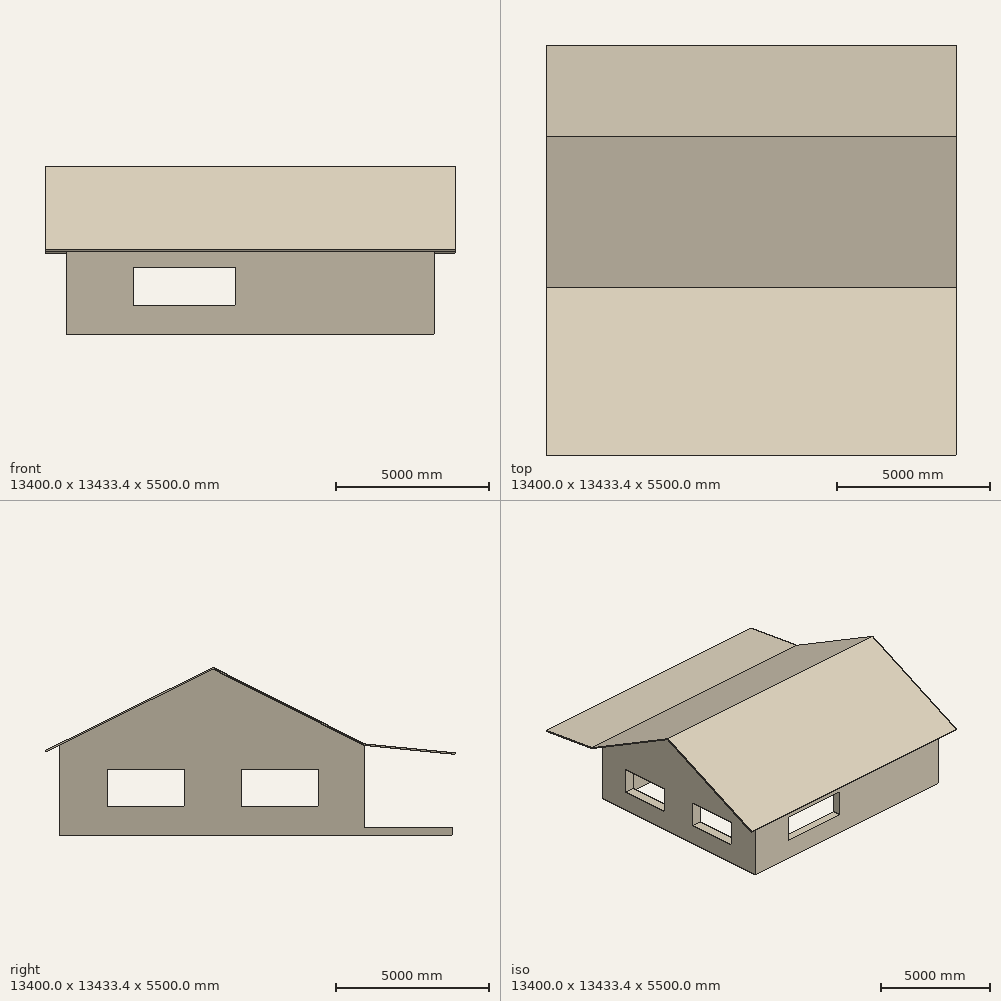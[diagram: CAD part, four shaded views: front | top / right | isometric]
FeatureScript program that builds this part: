
annotation { "Feature Type Name" : "Feature", "Feature Type Description" : "" }
export const myFeature = defineFeature(function(context is Context, id is Id, definition is map)
    precondition{}
    {
        {
            var Q0;
            Q0=qCreatedBy(makeId("Right.planeOp"),FACE);
            var sketch = newSketch(context, id + "F0", { "sketchPlane" : qUnion([Q0])});
            skLineSegment(sketch, "E0.bottom", {"start": v(-5048.67, 0) * mm, "end": v(4951.33, 0) * mm});
            skLineSegment(sketch, "E0.top", {"start": v(-5048.67, 0) * mm, "end": v(4951.33, 0) * mm});
            skLineSegment(sketch, "E0.left", {"start": v(-5048.67, 0) * mm, "end": v(-5048.67, 0) * mm});
            skLineSegment(sketch, "E0.right", {"start": v(4951.33, 0) * mm, "end": v(4951.33, 0) * mm});
            skLineSegment(sketch, "E1", {"start": v(4951.33, 250) * mm, "end": v(4951.33, 2949.75) * mm});
            skLineSegment(sketch, "E2", {"start": v(4951.33, 3000) * mm, "end": v(0, 5500) * mm});
            skLineSegment(sketch, "E3", {"start": v(0, 5500) * mm, "end": v(-5048.67, 3000) * mm});
            skLineSegment(sketch, "E4", {"start": v(-5048.67, 2944.2) * mm, "end": v(-5048.67, 0) * mm});
            skLineSegment(sketch, "E5", {"start": v(-5048.67, 3000) * mm, "end": v(-5496.74, 2778.12) * mm});
            skLineSegment(sketch, "E6", {"start": v(-5496.74, 2778.12) * mm, "end": v(-5474.56, 2733.32) * mm});
            skLineSegment(sketch, "E7", {"start": v(-5474.56, 2733.32) * mm, "end": v(-5048.67, 2944.2) * mm});
            skLineSegment(sketch, "E8", {"start": v(4951.33, 3000) * mm, "end": v(7936.67, 2703.75) * mm});
            skLineSegment(sketch, "E9", {"start": v(7936.67, 2703.75) * mm, "end": v(7931.73, 2654) * mm});
            skLineSegment(sketch, "E10", {"start": v(7931.73, 2654) * mm, "end": v(4951.33, 2949.75) * mm});
            skLineSegment(sketch, "E11", {"start": v(4951.33, 0) * mm, "end": v(7851.33, 0) * mm});
            skLineSegment(sketch, "E12", {"start": v(7851.33, 0) * mm, "end": v(7851.33, 250) * mm});
            skLineSegment(sketch, "E13", {"start": v(7851.33, 250) * mm, "end": v(4951.33, 250) * mm});
            skSolve(sketch);
        }
        {
            var Q0;
            Q0 = qSketchRegion(id + "F0", true);
            extrude(context, id + "F1", {"entities" : qUnion([Q0]), "depth" : 12000 * mm, "offsetDistance" : 25 * mm});
        }
        {
            var Q0;
            Q0=makeQuery(id+"F1.opExtrude","SWEPT_FACE",FACE,{"disambiguationData":[OSD([sQuery(id+"F0.wireOp",EDGE,"E0.top"),sQuery(id+"F0.wireOp",EDGE,"E11")])]});
            var sketch = newSketch(context, id + "F2", { "sketchPlane" : qUnion([Q0])});
            skLineSegment(sketch, "E14", {"start": v(0, -7851.33) * mm, "end": v(0, -4951.33) * mm});
            skLineSegment(sketch, "E15", {"start": v(0, -4951.33) * mm, "end": v(5000, -4951.33) * mm});
            skLineSegment(sketch, "E16", {"start": v(5000, -4951.33) * mm, "end": v(5000, -7851.33) * mm});
            skLineSegment(sketch, "E17", {"start": v(5000, -7851.33) * mm, "end": v(0, -7851.33) * mm});
            skSolve(sketch);
        }
        {
            var Q0;
            Q0 = qSketchRegion(id + "F2", true);
            extrude(context, id + "F3", {"entities" : qUnion([Q0]), "operationType" : NewBodyOperationType.REMOVE, "oppositeDirection" : true, "depth" : 250 * mm, "offsetDistance" : 25 * mm});
        }
        {
            var Q0;
            Q0=makeQuery(id+"F1.opExtrude","CAP_FACE",FACE,{"disambiguationData":[OSD([sQuery(id+"F0.wireOp",EDGE,"E0.top"),sQuery(id+"F0.wireOp",EDGE,"E1"),sQuery(id+"F0.wireOp",EDGE,"E2"),sQuery(id+"F0.wireOp",EDGE,"E3"),sQuery(id+"F0.wireOp",EDGE,"E4"),sQuery(id+"F0.wireOp",EDGE,"E5"),sQuery(id+"F0.wireOp",EDGE,"E6"),sQuery(id+"F0.wireOp",EDGE,"E7"),sQuery(id+"F0.wireOp",EDGE,"E8"),sQuery(id+"F0.wireOp",EDGE,"E9"),sQuery(id+"F0.wireOp",EDGE,"E10"),sQuery(id+"F0.wireOp",EDGE,"E11"),sQuery(id+"F0.wireOp",EDGE,"E12"),sQuery(id+"F0.wireOp",EDGE,"E13")])],"isStart":true});
            var sketch = newSketch(context, id + "F4", { "sketchPlane" : qUnion([Q0])});
            skLineSegment(sketch, "E18", {"start": v(5496.74, 2778.12) * mm, "end": v(0, 5500) * mm});
            skLineSegment(sketch, "E19", {"start": v(0, 5500) * mm, "end": v(-4951.33, 3000) * mm});
            skLineSegment(sketch, "E20", {"start": v(-4951.33, 3000) * mm, "end": v(-7936.67, 2703.75) * mm});
            skLineSegment(sketch, "E21", {"start": v(-7936.67, 2703.75) * mm, "end": v(-7931.73, 2654) * mm});
            skLineSegment(sketch, "E22", {"start": v(-7931.73, 2654) * mm, "end": v(-4951.33, 2949.75) * mm});
            skLineSegment(sketch, "E23", {"start": v(-4951.33, 2949.75) * mm, "end": v(0, 5449.75) * mm});
            skLineSegment(sketch, "E24", {"start": v(0, 5449.75) * mm, "end": v(5474.56, 2733.32) * mm});
            skLineSegment(sketch, "E25", {"start": v(5474.56, 2733.32) * mm, "end": v(5496.74, 2778.12) * mm});
            skSolve(sketch);
        }
        {
            var Q0;
            Q0 = qSketchRegion(id + "F4", true);
            extrude(context, id + "F5", {"entities" : qUnion([Q0]), "operationType" : NewBodyOperationType.ADD, "depth" : 700 * mm, "offsetDistance" : 25 * mm});
        }
        {
            var Q0;
            Q0=makeQuery(id+"F1.opExtrude","CAP_FACE",FACE,{"disambiguationData":[OSD([sQuery(id+"F0.wireOp",EDGE,"E0.top"),sQuery(id+"F0.wireOp",EDGE,"E1"),sQuery(id+"F0.wireOp",EDGE,"E2"),sQuery(id+"F0.wireOp",EDGE,"E3"),sQuery(id+"F0.wireOp",EDGE,"E4"),sQuery(id+"F0.wireOp",EDGE,"E5"),sQuery(id+"F0.wireOp",EDGE,"E6"),sQuery(id+"F0.wireOp",EDGE,"E7"),sQuery(id+"F0.wireOp",EDGE,"E8"),sQuery(id+"F0.wireOp",EDGE,"E9"),sQuery(id+"F0.wireOp",EDGE,"E10"),sQuery(id+"F0.wireOp",EDGE,"E11"),sQuery(id+"F0.wireOp",EDGE,"E12"),sQuery(id+"F0.wireOp",EDGE,"E13")])],"isStart":false});
            var sketch = newSketch(context, id + "F6", { "sketchPlane" : qUnion([Q0])});
            skLineSegment(sketch, "E26", {"start": v(-5474.56, 2733.32) * mm, "end": v(-5496.74, 2778.12) * mm});
            skLineSegment(sketch, "E27", {"start": v(-5496.74, 2778.12) * mm, "end": v(0, 5500) * mm});
            skLineSegment(sketch, "E28", {"start": v(0, 5500) * mm, "end": v(4951.33, 3000) * mm});
            skLineSegment(sketch, "E29", {"start": v(4951.33, 3000) * mm, "end": v(7936.67, 2703.75) * mm});
            skLineSegment(sketch, "E30", {"start": v(7936.67, 2703.75) * mm, "end": v(7931.73, 2654) * mm});
            skLineSegment(sketch, "E31", {"start": v(7931.73, 2654) * mm, "end": v(4951.33, 2949.75) * mm});
            skLineSegment(sketch, "E32", {"start": v(4951.33, 2949.75) * mm, "end": v(0, 5449.75) * mm});
            skLineSegment(sketch, "E33", {"start": v(0, 5449.75) * mm, "end": v(-5474.56, 2733.32) * mm});
            skSolve(sketch);
        }
        {
            var Q0;
            Q0 = qSketchRegion(id + "F6", true);
            extrude(context, id + "F7", {"entities" : qUnion([Q0]), "operationType" : NewBodyOperationType.ADD, "depth" : 700 * mm, "offsetDistance" : 25 * mm});
        }
        {
            var Q0;
            Q0=makeQuery(id+"F1.opExtrude","SWEPT_FACE",FACE,{"disambiguationData":[OSD([sQuery(id+"F0.wireOp",EDGE,"E0.top"),sQuery(id+"F0.wireOp",EDGE,"E11")])]});
            var sketch = newSketch(context, id + "F8", { "sketchPlane" : qUnion([Q0])});
            skLineSegment(sketch, "E34.bottom", {"start": v(500, 4648.67) * mm, "end": v(11500, 4648.67) * mm});
            skLineSegment(sketch, "E34.top", {"start": v(500, -4451.33) * mm, "end": v(11500, -4451.33) * mm});
            skLineSegment(sketch, "E34.left", {"start": v(500, 4648.67) * mm, "end": v(500, -4451.33) * mm});
            skLineSegment(sketch, "E34.right", {"start": v(11500, 4648.67) * mm, "end": v(11500, -4451.33) * mm});
            skSolve(sketch);
        }
        {
            var Q0;
            Q0 = qSketchRegion(id + "F8", true);
            extrude(context, id + "F9", {"entities" : qUnion([Q0]), "operationType" : NewBodyOperationType.REMOVE, "oppositeDirection" : true, "depth" : 2950 * mm, "offsetDistance" : 25 * mm});
        }
        {
            var Q0;
            Q0=makeQuery(id+"F1.opExtrude","CAP_FACE",FACE,{"disambiguationData":[OSD([sQuery(id+"F0.wireOp",EDGE,"E0.top"),sQuery(id+"F0.wireOp",EDGE,"E1"),sQuery(id+"F0.wireOp",EDGE,"E2"),sQuery(id+"F0.wireOp",EDGE,"E3"),sQuery(id+"F0.wireOp",EDGE,"E4"),sQuery(id+"F0.wireOp",EDGE,"E5"),sQuery(id+"F0.wireOp",EDGE,"E6"),sQuery(id+"F0.wireOp",EDGE,"E7"),sQuery(id+"F0.wireOp",EDGE,"E8"),sQuery(id+"F0.wireOp",EDGE,"E9"),sQuery(id+"F0.wireOp",EDGE,"E10"),sQuery(id+"F0.wireOp",EDGE,"E11"),sQuery(id+"F0.wireOp",EDGE,"E12"),sQuery(id+"F0.wireOp",EDGE,"E13")])],"isStart":true});
            var sketch = newSketch(context, id + "F10", { "sketchPlane" : qUnion([Q0])});
            skLineSegment(sketch, "E35.bottom", {"start": v(-3453.27, 949.36) * mm, "end": v(-933.16, 949.36) * mm});
            skLineSegment(sketch, "E35.top", {"start": v(-3453.27, 2162.4) * mm, "end": v(-933.16, 2162.4) * mm});
            skLineSegment(sketch, "E35.left", {"start": v(-3453.27, 949.36) * mm, "end": v(-3453.27, 2162.4) * mm});
            skLineSegment(sketch, "E35.right", {"start": v(-933.16, 949.36) * mm, "end": v(-933.16, 2162.4) * mm});
            skLineSegment(sketch, "E36.MirrorCS", {"start": v(3453.27, 949.36) * mm, "end": v(3453.27, 2162.4) * mm});
            skLineSegment(sketch, "E37.MirrorCS", {"start": v(933.16, 949.36) * mm, "end": v(933.16, 2162.4) * mm});
            skLineSegment(sketch, "E38.MirrorCS", {"start": v(3453.27, 949.36) * mm, "end": v(933.16, 949.36) * mm});
            skLineSegment(sketch, "E39.MirrorCS", {"start": v(3453.27, 2162.4) * mm, "end": v(933.16, 2162.4) * mm});
            skSolve(sketch);
        }
        {
            var Q0;
            Q0 = qSketchRegion(id + "F10", true);
            extrude(context, id + "F11", {"entities" : qUnion([Q0]), "operationType" : NewBodyOperationType.REMOVE, "oppositeDirection" : true, "depth" : 12000 * mm, "offsetDistance" : 25 * mm});
        }
        {
            var Q0;
            Q0=makeQuery(id+"F1.opExtrude","SWEPT_FACE",FACE,{"disambiguationData":[OSD([sQuery(id+"F0.wireOp",EDGE,"E4")])]});
            var sketch = newSketch(context, id + "F12", { "sketchPlane" : qUnion([Q0])});
            skLineSegment(sketch, "E40.bottom", {"start": v(2167.56, 2201.24) * mm, "end": v(5521.46, 2201.24) * mm});
            skLineSegment(sketch, "E40.top", {"start": v(2167.56, 966.02) * mm, "end": v(5521.46, 966.02) * mm});
            skLineSegment(sketch, "E40.left", {"start": v(2167.56, 2201.24) * mm, "end": v(2167.56, 966.02) * mm});
            skLineSegment(sketch, "E40.right", {"start": v(5521.46, 2201.24) * mm, "end": v(5521.46, 966.02) * mm});
            skSolve(sketch);
        }
        {
            var Q0;
            Q0 = qSketchRegion(id + "F12", true);
            extrude(context, id + "F13", {"entities" : qUnion([Q0]), "operationType" : NewBodyOperationType.REMOVE, "oppositeDirection" : true, "depth" : 10000 * mm, "offsetDistance" : 25 * mm});
        }
        {
            var Q0;
            Q0=makeQuery(id+"F3.boolean.opBoolean","MERGE",FACE,{"derivedFrom":[makeQuery(id+"F1.opExtrude","SWEPT_FACE",FACE,{"disambiguationData":[OSD([sQuery(id+"F0.wireOp",EDGE,"E1")])]})],"fromTools":[makeQuery(id+"F3.opExtrude","SWEPT_FACE",FACE,{"disambiguationData":[OSD([sQuery(id+"F2.wireOp",EDGE,"E15")])]})]});
            var sketch = newSketch(context, id + "F14", { "sketchPlane" : qUnion([Q0])});
            skLineSegment(sketch, "E41.bottom", {"start": v(-8500, 250) * mm, "end": v(-8500, 250) * mm});
            skLineSegment(sketch, "E41.top", {"start": v(-8500, 2201.29) * mm, "end": v(-8500, 2201.29) * mm});
            skLineSegment(sketch, "E42.bottom", {"start": v(-9428.39, 2201.29) * mm, "end": v(-7927.59, 2201.29) * mm});
            skLineSegment(sketch, "E42.top", {"start": v(-9428.39, 250) * mm, "end": v(-7927.59, 250) * mm});
            skLineSegment(sketch, "E42.left", {"start": v(-9428.39, 2201.29) * mm, "end": v(-9428.39, 250) * mm});
            skLineSegment(sketch, "E42.right", {"start": v(-7927.59, 2201.29) * mm, "end": v(-7927.59, 250) * mm});
            skSolve(sketch);
        }
        {
            var Q0;
            Q0 = qSketchRegion(id + "F14", true);
            extrude(context, id + "F15", {"entities" : qUnion([Q0]), "operationType" : NewBodyOperationType.REMOVE, "oppositeDirection" : true, "depth" : 500 * mm, "offsetDistance" : 25 * mm});
        }
    });
